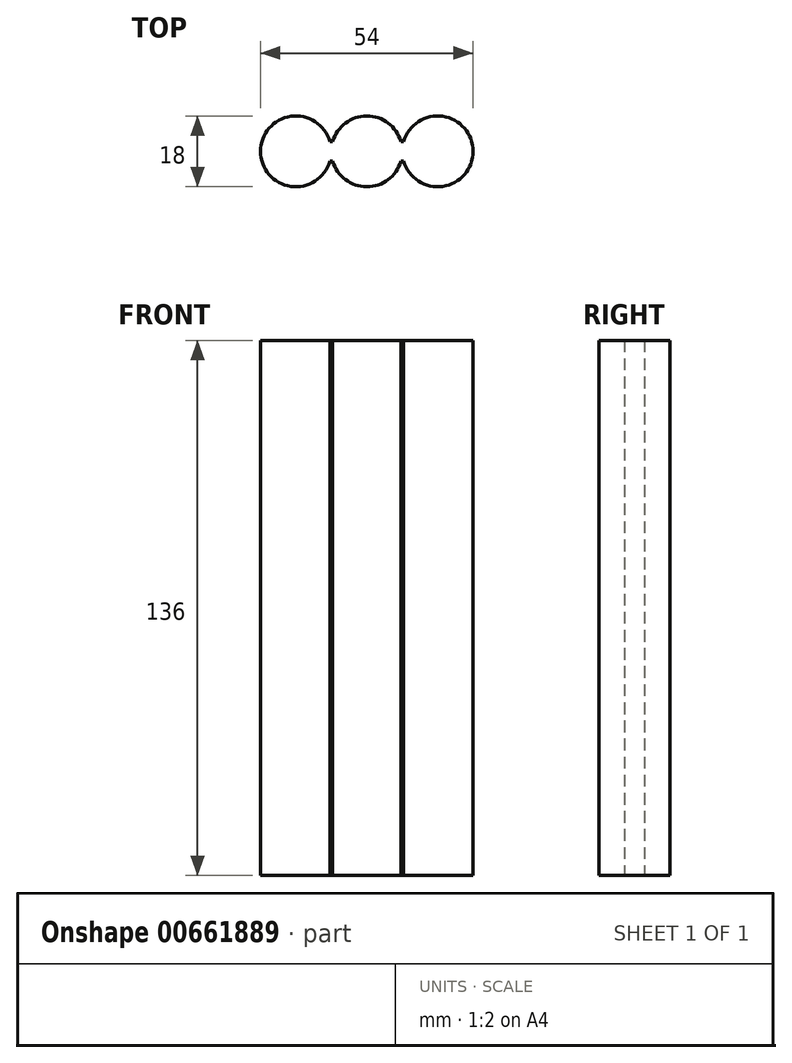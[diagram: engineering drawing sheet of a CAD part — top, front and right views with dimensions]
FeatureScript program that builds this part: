
annotation { "Feature Type Name" : "Feature", "Feature Type Description" : "" }
export const myFeature = defineFeature(function(context is Context, id is Id, definition is map)
    precondition{}
    {
        {
            var Q0;
            Q0=qCreatedBy(makeId("Top.planeOp"),FACE);
            var sketch = newSketch(context, id + "F0", { "sketchPlane" : qUnion([Q0])});
            skCircle(sketch, "E0", {"center": v(-18, 0) * mm, "radius": 9 * mm});
            skLineSegment(sketch, "E1", {"start": v(0, 0) * mm, "end": v(0, -36) * mm, "construction": true});
            skCircle(sketch, "E2.MirrorC", {"center": v(18, 0) * mm, "radius": 9 * mm});
            skLineSegment(sketch, "E3", {"start": v(-18, 9) * mm, "end": v(18, 9) * mm, "construction": true});
            skPoint(sketch, "E4", {"position": v(0, 9) * mm});
            skCircle(sketch, "E5", {"center": v(0, 0) * mm, "radius": 9 * mm});
            skSolve(sketch);
        }
        {
            var Q0;
            Q0 = qSketchRegion(id + "F0", true);
            extrude(context, id + "F1", {"entities" : qUnion([Q0]), "depth" : (68 * 2) * mm, "offsetDistance" : 25 * mm, "symmetric" : true});
        }
        {
            var Q0;
            Q0=qCreatedBy(makeId("Top.planeOp"),FACE);
            var sketch = newSketch(context, id + "F2", { "sketchPlane" : qUnion([Q0])});
            skLineSegment(sketch, "E6.bottom", {"start": v(20, -2.5) * mm, "end": v(-20, -2.5) * mm});
            skLineSegment(sketch, "E6.top", {"start": v(20, 2.5) * mm, "end": v(-20, 2.5) * mm});
            skLineSegment(sketch, "E6.left", {"start": v(20, -2.5) * mm, "end": v(20, 2.5) * mm});
            skLineSegment(sketch, "E6.right", {"start": v(-20, -2.5) * mm, "end": v(-20, 2.5) * mm});
            skPoint(sketch, "E6.middle", {"position": v(0, 0) * mm});
            skSolve(sketch);
        }
        {
            var Q0;
            Q0 = qSketchRegion(id + "F2", true);
            var Q1;
            Q1=makeQuery(id+"F1.opExtrude","CAP_FACE",FACE,{"disambiguationData":[OSD([sQuery(id+"F0.wireOp",EDGE,"E5")])],"isStart":false});
            var Q2;
            Q2=makeQuery(id+"F1.opExtrude","CAP_FACE",FACE,{"disambiguationData":[OSD([sQuery(id+"F0.wireOp",EDGE,"E5")])],"isStart":true});
            extrude(context, id + "F3", {"entities" : qUnion([Q0]), "operationType" : NewBodyOperationType.ADD, "endBound" : BoundingType.UP_TO_SURFACE, "depth" : 50 * mm, "endBoundEntityFace" : qUnion([Q1]), "offsetDistance" : 25 * mm, "hasSecondDirection" : true, "secondDirectionBound" : BoundingType.UP_TO_SURFACE, "secondDirectionOppositeDirection" : true, "secondDirectionDepth" : 25 * mm, "secondDirectionBoundEntityFace" : qUnion([Q2])});
        }
        {
            var Q0;
            Q0=sQuery(id+"F0.wireOp",VERTEX,"E4");
            var Q1;
            Q1=qCreatedBy(makeId("Front.planeOp"),FACE);
            cPlane(context, id + "F4", {"entities" : qUnion([Q0, Q1]), "cplaneType" : CPlaneType.PLANE_POINT, "offset" : 25 * mm, "width" : 150 * mm, "height" : 150 * mm});
        }
        {
            var Q0;
            Q0=qCreatedBy(id+"F4.planeOp",FACE);
            var sketch = newSketch(context, id + "F5", { "sketchPlane" : qUnion([Q0])});
            skCircle(sketch, "E7", {"center": v(0, 0) * mm, "radius": 12.5 * mm});
            skSolve(sketch);
        }
    });
